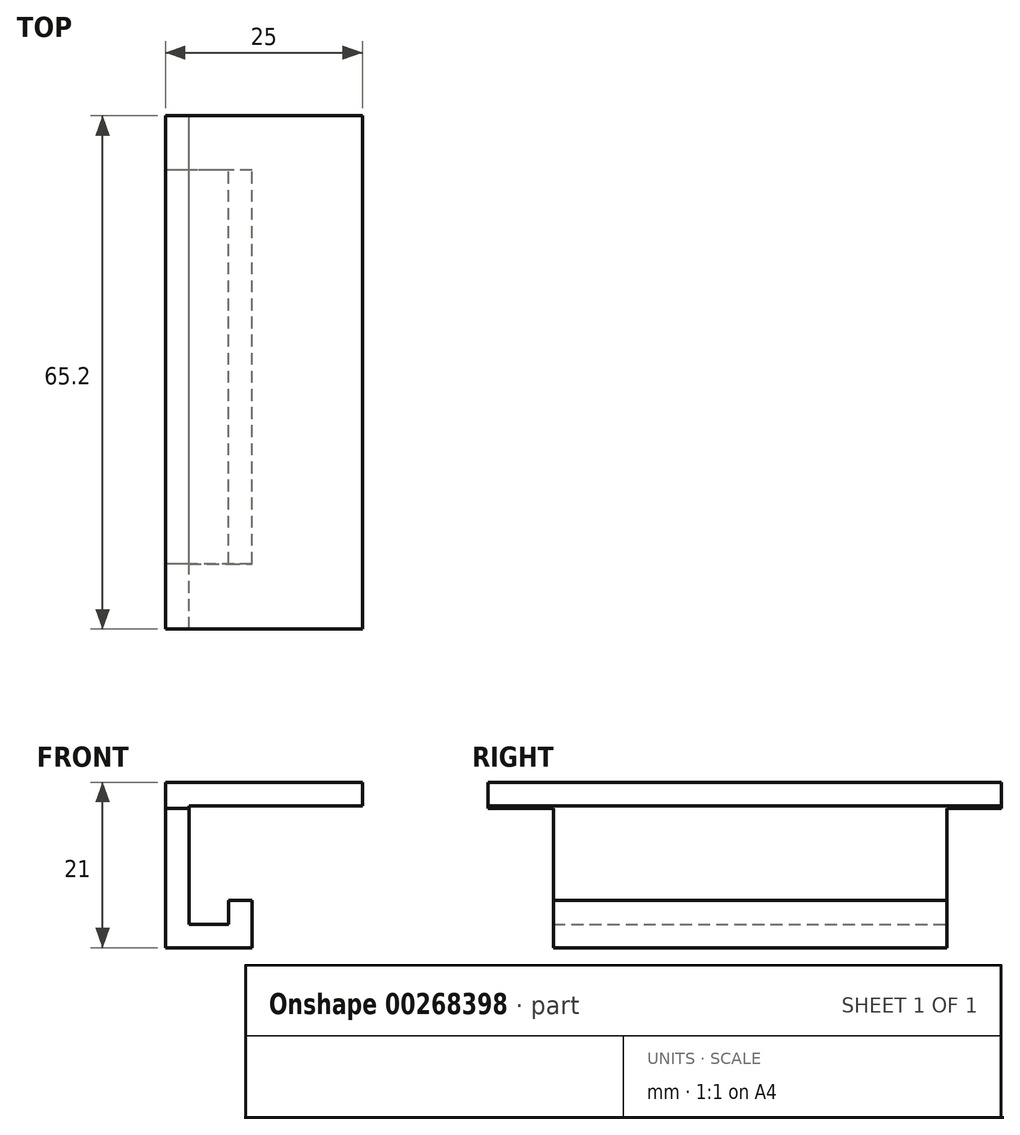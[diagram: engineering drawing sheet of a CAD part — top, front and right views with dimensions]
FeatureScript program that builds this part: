
annotation { "Feature Type Name" : "Feature", "Feature Type Description" : "" }
export const myFeature = defineFeature(function(context is Context, id is Id, definition is map)
    precondition{}
    {
        {
            var Q0;
            Q0=qCreatedBy(makeId("Front.planeOp"),FACE);
            var sketch = newSketch(context, id + "F0", { "sketchPlane" : qUnion([Q0])});
            skLineSegment(sketch, "E0", {"start": v(-27.6, 15) * mm, "end": v(-27.6, 12) * mm});
            skLineSegment(sketch, "E1", {"start": v(-27.6, 12) * mm, "end": v(-59.6, 12) * mm});
            skLineSegment(sketch, "E2", {"start": v(-59.6, 12) * mm, "end": v(-59.6, -3) * mm});
            skLineSegment(sketch, "E3", {"start": v(-59.6, -3) * mm, "end": v(-54.6, -3) * mm});
            skLineSegment(sketch, "E4", {"start": v(-51.6, 0) * mm, "end": v(-51.6, -6) * mm});
            skLineSegment(sketch, "E5", {"start": v(-51.6, -6) * mm, "end": v(-62.6, -6) * mm});
            skLineSegment(sketch, "E6", {"start": v(-62.6, -6) * mm, "end": v(-62.6, 15) * mm});
            skLineSegment(sketch, "E7", {"start": v(-62.6, 15) * mm, "end": v(-27.6, 15) * mm});
            skLineSegment(sketch, "E8", {"start": v(-54.6, -3) * mm, "end": v(-54.6, 0) * mm});
            skLineSegment(sketch, "E9", {"start": v(-54.6, 0) * mm, "end": v(-51.6, 0) * mm});
            skSolve(sketch);
        }
        {
            var Q0;
            Q0=makeQuery(id+"F0.imprint","IMPRINT",FACE,{"disambiguationData":[TD([[makeQuery(id+"F0.imprint","IMPRINT",EDGE,{"derivedFrom":sQuery(id+"F0.wireOp",EDGE,"E0")}),-1.0]])]});
            extrude(context, id + "F1", {"entities" : qUnion([Q0]), "depth" : 65.2 * mm});
        }
        {
            var Q0;
            Q0=makeQuery(id+"F1.opExtrude","SWEPT_FACE",FACE,{"disambiguationData":[OSD([sQuery(id+"F0.wireOp",EDGE,"E6")])]});
            var sketch = newSketch(context, id + "F2", { "sketchPlane" : qUnion([Q0])});
            skLineSegment(sketch, "E10", {"start": v(0, 11.7) * mm, "end": v(6.92, 11.7) * mm});
            skLineSegment(sketch, "E11", {"start": v(6.92, 11.7) * mm, "end": v(6.92, -6) * mm});
            skLineSegment(sketch, "E12", {"start": v(56.92, -6) * mm, "end": v(56.92, 11.7) * mm});
            skLineSegment(sketch, "E13", {"start": v(56.92, 11.7) * mm, "end": v(65.2, 11.7) * mm});
            skLineSegment(sketch, "E14", {"start": v(65.2, 11.7) * mm, "end": v(65.2, 15) * mm});
            skLineSegment(sketch, "E15", {"start": v(65.2, 15) * mm, "end": v(0, 15) * mm});
            skLineSegment(sketch, "E16", {"start": v(0, 15) * mm, "end": v(0, 11.7) * mm});
            skLineSegment(sketch, "E17", {"start": v(65.2, -6) * mm, "end": v(0, 15) * mm, "construction": true});
            skLineSegment(sketch, "E18", {"start": v(0, -6) * mm, "end": v(65.2, 15) * mm, "construction": true});
            skPoint(sketch, "E19", {"position": v(32.6, 4.5) * mm});
            skLineSegment(sketch, "E20", {"start": v(32.6, -21.24) * mm, "end": v(32.6, 30.24) * mm, "construction": true});
            skLineSegment(sketch, "E21", {"start": v(56.92, -6) * mm, "end": v(32.6, -6) * mm});
            skSolve(sketch);
        }
        {
            var Q0;
            Q0 = qSketchRegion(id + "F2", true);
            var Q1;
            Q1=makeQuery(id+"F2.imprint","IMPRINT",FACE,{"disambiguationData":[TD([[makeQuery(id+"F2.imprint","IMPRINT",EDGE,{"derivedFrom":sQuery(id+"F2.wireOp",EDGE,"E10")}),1.0]])]});
            extrude(context, id + "F3", {"entities" : qUnion([Q0, Q1]), "operationType" : NewBodyOperationType.INTERSECT, "oppositeDirection" : true, "depth" : 25 * mm});
        }
    });
